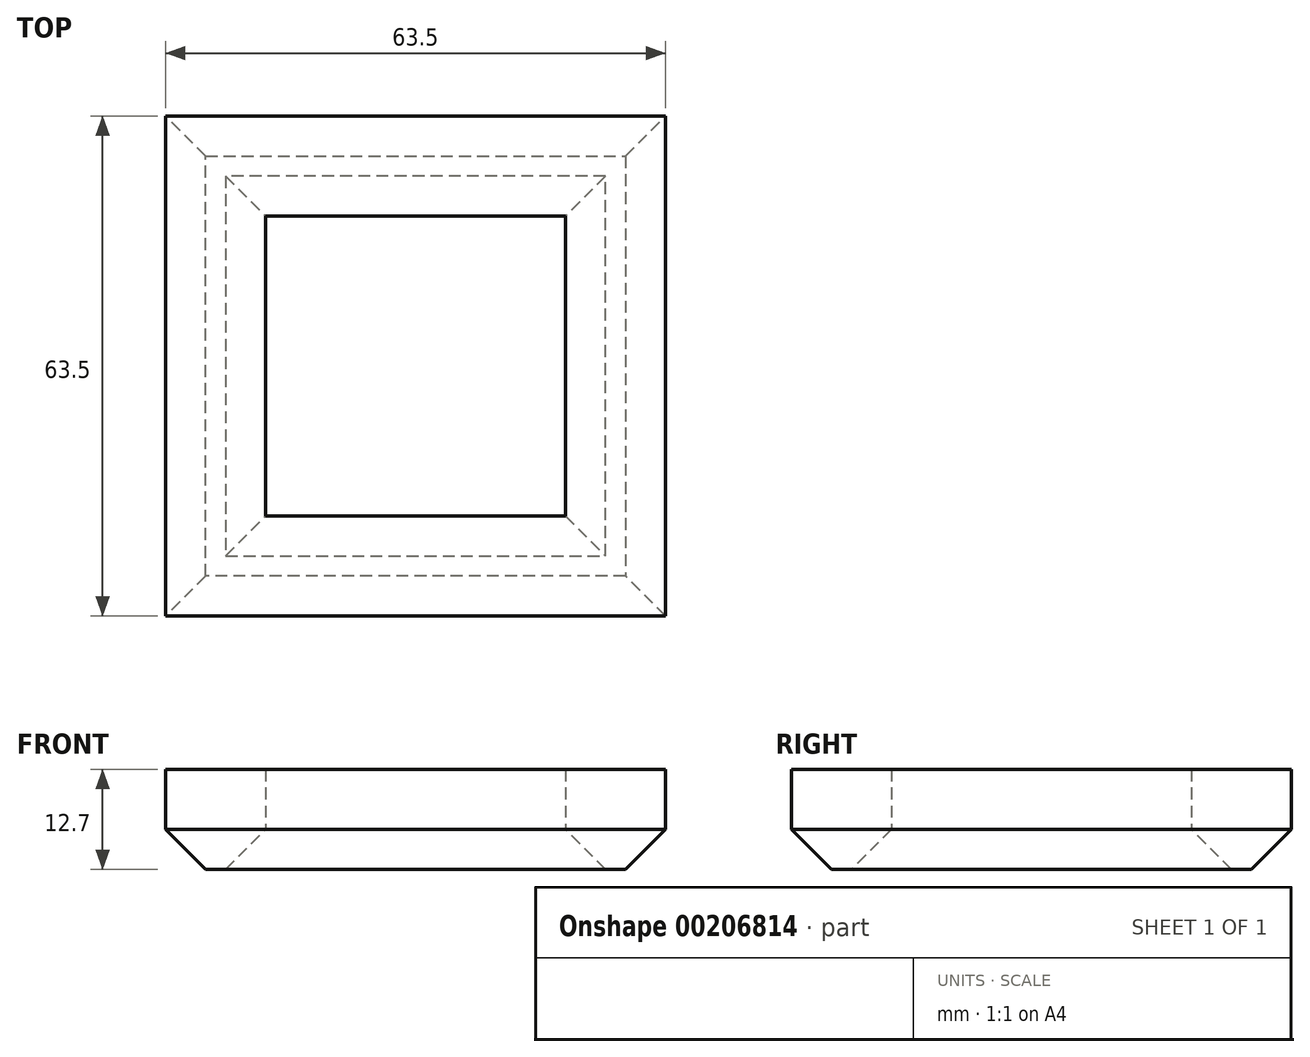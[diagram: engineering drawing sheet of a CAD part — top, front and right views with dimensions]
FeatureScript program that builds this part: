
annotation { "Feature Type Name" : "Feature", "Feature Type Description" : "" }
export const myFeature = defineFeature(function(context is Context, id is Id, definition is map)
    precondition{}
    {
        {
            var Q0;
            Q0=qCreatedBy(makeId("Top.planeOp"),FACE);
            var sketch = newSketch(context, id + "F0", { "sketchPlane" : qUnion([Q0])});
            skLineSegment(sketch, "E0.bottom", {"start": v(31.75, -31.75) * mm, "end": v(-31.75, -31.75) * mm});
            skLineSegment(sketch, "E0.top", {"start": v(31.75, 31.75) * mm, "end": v(-31.75, 31.75) * mm});
            skLineSegment(sketch, "E0.left", {"start": v(31.75, -31.75) * mm, "end": v(31.75, 31.75) * mm});
            skLineSegment(sketch, "E0.right", {"start": v(-31.75, -31.75) * mm, "end": v(-31.75, 31.75) * mm});
            skPoint(sketch, "E0.middle", {"position": v(0, 0) * mm});
            skLineSegment(sketch, "E1.0", {"start": v(19.05, 19.05) * mm, "end": v(-19.05, 19.05) * mm});
            skLineSegment(sketch, "E1.1", {"start": v(19.05, -19.05) * mm, "end": v(19.05, 19.05) * mm});
            skLineSegment(sketch, "E1.2", {"start": v(19.05, -19.05) * mm, "end": v(-19.05, -19.05) * mm});
            skLineSegment(sketch, "E1.3", {"start": v(-19.05, -19.05) * mm, "end": v(-19.05, 19.05) * mm});
            skSolve(sketch);
        }
        {
            var Q0;
            Q0 = qSketchRegion(id + "F0", true);
            extrude(context, id + "F1", {"entities" : qUnion([Q0]), "depth" : 12.7 * mm});
        }
        {
            var Q0;
            Q0=makeQuery(id+"F1.opExtrude","CAP_EDGE",EDGE,{"disambiguationData":[OSD([sQuery(id+"F0.wireOp",EDGE,"E1.1")])],"isStart":true});
            var Q1;
            Q1=makeQuery(id+"F1.opExtrude","CAP_EDGE",EDGE,{"disambiguationData":[OSD([sQuery(id+"F0.wireOp",EDGE,"E1.0")])],"isStart":true});
            var Q2;
            Q2=makeQuery(id+"F1.opExtrude","CAP_EDGE",EDGE,{"disambiguationData":[OSD([sQuery(id+"F0.wireOp",EDGE,"E1.3")])],"isStart":true});
            var Q3;
            Q3=makeQuery(id+"F1.opExtrude","CAP_EDGE",EDGE,{"disambiguationData":[OSD([sQuery(id+"F0.wireOp",EDGE,"E1.2")])],"isStart":true});
            chamfer(context, id + "F2", {"entities" : qUnion([Q0, Q1, Q2, Q3]), "width" : 5.08 * mm, "tangentPropagation" : true});
        }
        {
            var Q0;
            Q0=makeQuery(id+"F1.opExtrude","CAP_EDGE",EDGE,{"disambiguationData":[OSD([sQuery(id+"F0.wireOp",EDGE,"E0.top")])],"isStart":true});
            var Q1;
            Q1=makeQuery(id+"F1.opExtrude","CAP_EDGE",EDGE,{"disambiguationData":[OSD([sQuery(id+"F0.wireOp",EDGE,"E0.right")])],"isStart":true});
            var Q2;
            Q2=makeQuery(id+"F1.opExtrude","CAP_EDGE",EDGE,{"disambiguationData":[OSD([sQuery(id+"F0.wireOp",EDGE,"E0.bottom")])],"isStart":true});
            var Q3;
            Q3=makeQuery(id+"F1.opExtrude","CAP_EDGE",EDGE,{"disambiguationData":[OSD([sQuery(id+"F0.wireOp",EDGE,"E0.left")])],"isStart":true});
            chamfer(context, id + "F3", {"entities" : qUnion([Q0, Q1, Q2, Q3]), "width" : 5.08 * mm, "tangentPropagation" : true});
        }
    });
